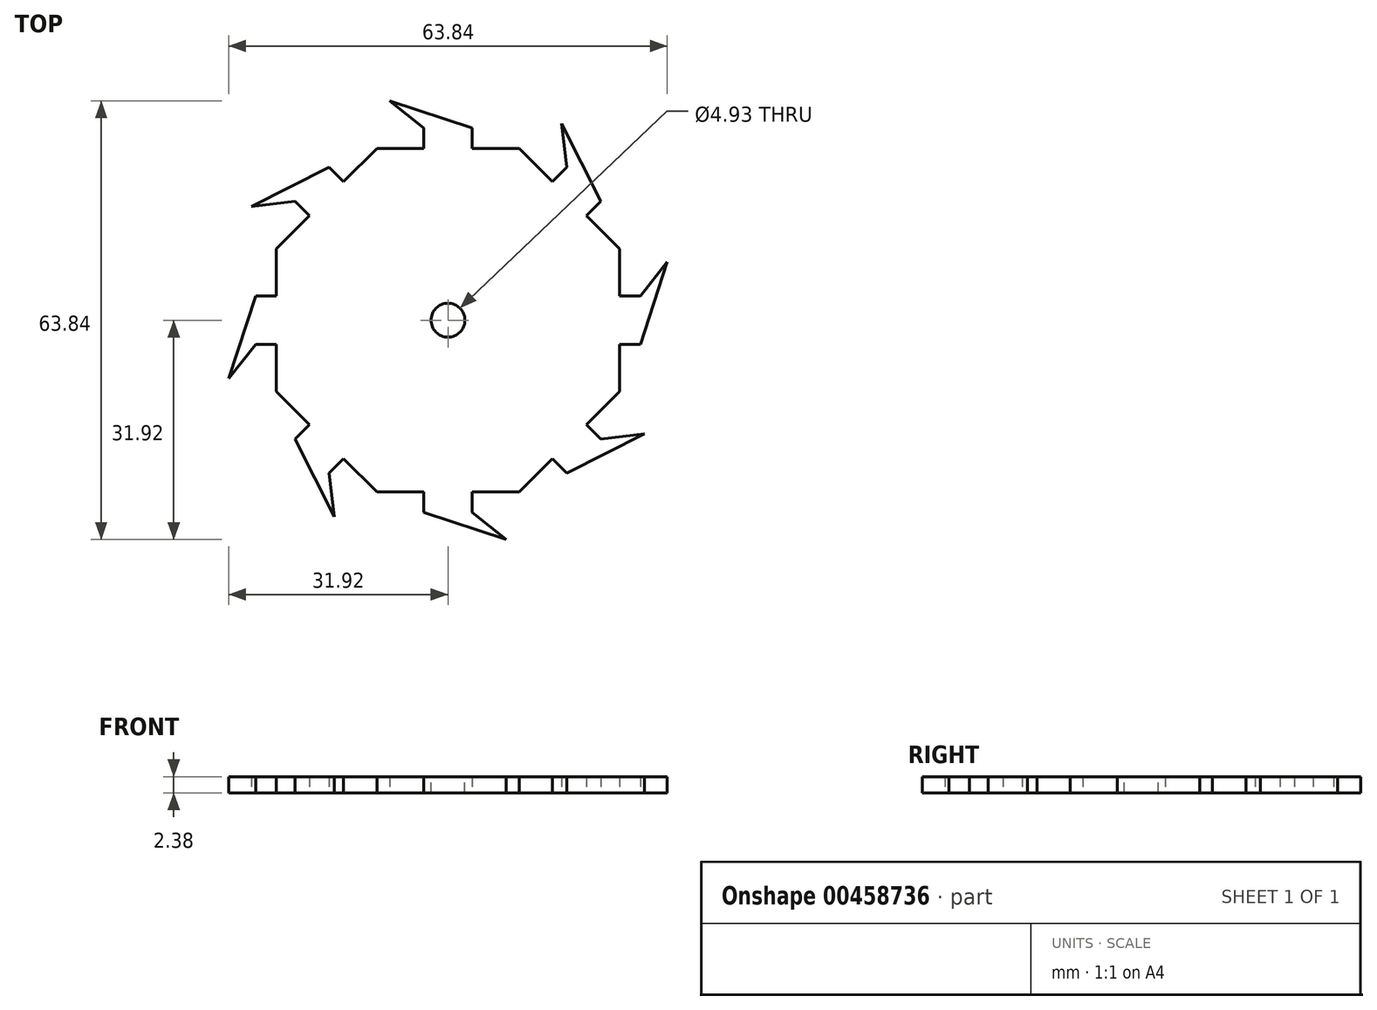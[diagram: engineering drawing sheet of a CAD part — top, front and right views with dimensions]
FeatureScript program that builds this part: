
annotation { "Feature Type Name" : "Feature", "Feature Type Description" : "" }
export const myFeature = defineFeature(function(context is Context, id is Id, definition is map)
    precondition{}
    {
        {
            var Q0;
            Q0=qCreatedBy(makeId("Top.planeOp"),FACE);
            var sketch = newSketch(context, id + "F0", { "sketchPlane" : qUnion([Q0])});
            skLineSegment(sketch, "E0", {"start": v(0, 0) * mm, "end": v(-10.36, 25) * mm});
            skLineSegment(sketch, "E1", {"start": v(0, 0) * mm, "end": v(10.36, 25) * mm});
            skLineSegment(sketch, "E2", {"start": v(-10.36, 25) * mm, "end": v(10.36, 25) * mm});
            skLineSegment(sketch, "E3.bottom", {"start": v(-3.5, 25) * mm, "end": v(3.5, 25) * mm});
            skLineSegment(sketch, "E3.top", {"start": v(-3.5, 28) * mm, "end": v(3.5, 28) * mm});
            skLineSegment(sketch, "E3.left", {"start": v(-3.5, 25) * mm, "end": v(-3.5, 28) * mm});
            skLineSegment(sketch, "E3.right", {"start": v(3.5, 25) * mm, "end": v(3.5, 28) * mm});
            skLineSegment(sketch, "E4", {"start": v(-3.5, 28) * mm, "end": v(-8.5, 31.92) * mm});
            skLineSegment(sketch, "E5", {"start": v(-8.5, 31.92) * mm, "end": v(3.5, 28) * mm});
            skLineSegment(sketch, "E6", {"start": v(0, 0) * mm, "end": v(0, 25) * mm});
            skLineSegment(sketch, "E7.1.0", {"start": v(0, 0) * mm, "end": v(-17.68, 17.68) * mm});
            skLineSegment(sketch, "E7.1.2", {"start": v(0, 0) * mm, "end": v(-25, 10.36) * mm});
            skLineSegment(sketch, "E7.1.3", {"start": v(-28.58, 16.56) * mm, "end": v(-17.32, 22.27) * mm});
            skLineSegment(sketch, "E7.1.4", {"start": v(-15.2, 20.15) * mm, "end": v(-17.32, 22.27) * mm});
            skLineSegment(sketch, "E7.1.5", {"start": v(-22.27, 17.32) * mm, "end": v(-28.58, 16.56) * mm});
            skLineSegment(sketch, "E7.1.6", {"start": v(-20.15, 15.2) * mm, "end": v(-22.27, 17.32) * mm});
            skLineSegment(sketch, "E7.1.7", {"start": v(-25, 10.36) * mm, "end": v(-10.36, 25) * mm});
            skLineSegment(sketch, "E7.1.8", {"start": v(-22.27, 17.32) * mm, "end": v(-17.32, 22.27) * mm});
            skLineSegment(sketch, "E7.1.9", {"start": v(-20.15, 15.2) * mm, "end": v(-15.2, 20.15) * mm});
            skLineSegment(sketch, "E7.2.0", {"start": v(0, 0) * mm, "end": v(-25, 0) * mm});
            skLineSegment(sketch, "E7.2.1", {"start": v(0, 0) * mm, "end": v(-25, 10.36) * mm});
            skLineSegment(sketch, "E7.2.2", {"start": v(0, 0) * mm, "end": v(-25, -10.36) * mm});
            skLineSegment(sketch, "E7.2.3", {"start": v(-31.92, -8.5) * mm, "end": v(-28, 3.5) * mm});
            skLineSegment(sketch, "E7.2.4", {"start": v(-25, 3.5) * mm, "end": v(-28, 3.5) * mm});
            skLineSegment(sketch, "E7.2.5", {"start": v(-28, -3.5) * mm, "end": v(-31.92, -8.5) * mm});
            skLineSegment(sketch, "E7.2.6", {"start": v(-25, -3.5) * mm, "end": v(-28, -3.5) * mm});
            skLineSegment(sketch, "E7.2.7", {"start": v(-25, -10.36) * mm, "end": v(-25, 10.36) * mm});
            skLineSegment(sketch, "E7.2.8", {"start": v(-28, -3.5) * mm, "end": v(-28, 3.5) * mm});
            skLineSegment(sketch, "E7.2.9", {"start": v(-25, -3.5) * mm, "end": v(-25, 3.5) * mm});
            skLineSegment(sketch, "E7.3.0", {"start": v(0, 0) * mm, "end": v(-17.68, -17.68) * mm});
            skLineSegment(sketch, "E7.3.1", {"start": v(0, 0) * mm, "end": v(-25, -10.36) * mm});
            skLineSegment(sketch, "E7.3.2", {"start": v(0, 0) * mm, "end": v(-10.36, -25) * mm});
            skLineSegment(sketch, "E7.3.3", {"start": v(-16.56, -28.58) * mm, "end": v(-22.27, -17.32) * mm});
            skLineSegment(sketch, "E7.3.4", {"start": v(-20.15, -15.2) * mm, "end": v(-22.27, -17.32) * mm});
            skLineSegment(sketch, "E7.3.5", {"start": v(-17.32, -22.27) * mm, "end": v(-16.56, -28.58) * mm});
            skLineSegment(sketch, "E7.3.6", {"start": v(-15.2, -20.15) * mm, "end": v(-17.32, -22.27) * mm});
            skLineSegment(sketch, "E7.3.7", {"start": v(-10.36, -25) * mm, "end": v(-25, -10.36) * mm});
            skLineSegment(sketch, "E7.3.8", {"start": v(-17.32, -22.27) * mm, "end": v(-22.27, -17.32) * mm});
            skLineSegment(sketch, "E7.3.9", {"start": v(-15.2, -20.15) * mm, "end": v(-20.15, -15.2) * mm});
            skLineSegment(sketch, "E7.4.0", {"start": v(0, 0) * mm, "end": v(0, -25) * mm});
            skLineSegment(sketch, "E7.4.1", {"start": v(0, 0) * mm, "end": v(-10.36, -25) * mm});
            skLineSegment(sketch, "E7.4.2", {"start": v(0, 0) * mm, "end": v(10.36, -25) * mm});
            skLineSegment(sketch, "E7.4.3", {"start": v(8.5, -31.92) * mm, "end": v(-3.5, -28) * mm});
            skLineSegment(sketch, "E7.4.4", {"start": v(-3.5, -25) * mm, "end": v(-3.5, -28) * mm});
            skLineSegment(sketch, "E7.4.5", {"start": v(3.5, -28) * mm, "end": v(8.5, -31.92) * mm});
            skLineSegment(sketch, "E7.4.6", {"start": v(3.5, -25) * mm, "end": v(3.5, -28) * mm});
            skLineSegment(sketch, "E7.4.7", {"start": v(10.36, -25) * mm, "end": v(-10.36, -25) * mm});
            skLineSegment(sketch, "E7.4.8", {"start": v(3.5, -28) * mm, "end": v(-3.5, -28) * mm});
            skLineSegment(sketch, "E7.4.9", {"start": v(3.5, -25) * mm, "end": v(-3.5, -25) * mm});
            skLineSegment(sketch, "E7.5.0", {"start": v(0, 0) * mm, "end": v(17.68, -17.68) * mm});
            skLineSegment(sketch, "E7.5.1", {"start": v(0, 0) * mm, "end": v(10.36, -25) * mm});
            skLineSegment(sketch, "E7.5.2", {"start": v(0, 0) * mm, "end": v(25, -10.36) * mm});
            skLineSegment(sketch, "E7.5.3", {"start": v(28.58, -16.56) * mm, "end": v(17.32, -22.27) * mm});
            skLineSegment(sketch, "E7.5.4", {"start": v(15.2, -20.15) * mm, "end": v(17.32, -22.27) * mm});
            skLineSegment(sketch, "E7.5.5", {"start": v(22.27, -17.32) * mm, "end": v(28.58, -16.56) * mm});
            skLineSegment(sketch, "E7.5.6", {"start": v(20.15, -15.2) * mm, "end": v(22.27, -17.32) * mm});
            skLineSegment(sketch, "E7.5.7", {"start": v(25, -10.36) * mm, "end": v(10.36, -25) * mm});
            skLineSegment(sketch, "E7.5.8", {"start": v(22.27, -17.32) * mm, "end": v(17.32, -22.27) * mm});
            skLineSegment(sketch, "E7.5.9", {"start": v(20.15, -15.2) * mm, "end": v(15.2, -20.15) * mm});
            skLineSegment(sketch, "E7.6.0", {"start": v(0, 0) * mm, "end": v(25, 0) * mm});
            skLineSegment(sketch, "E7.6.1", {"start": v(0, 0) * mm, "end": v(25, -10.36) * mm});
            skLineSegment(sketch, "E7.6.2", {"start": v(0, 0) * mm, "end": v(25, 10.36) * mm});
            skLineSegment(sketch, "E7.6.3", {"start": v(31.92, 8.5) * mm, "end": v(28, -3.5) * mm});
            skLineSegment(sketch, "E7.6.4", {"start": v(25, -3.5) * mm, "end": v(28, -3.5) * mm});
            skLineSegment(sketch, "E7.6.5", {"start": v(28, 3.5) * mm, "end": v(31.92, 8.5) * mm});
            skLineSegment(sketch, "E7.6.6", {"start": v(25, 3.5) * mm, "end": v(28, 3.5) * mm});
            skLineSegment(sketch, "E7.6.7", {"start": v(25, 10.36) * mm, "end": v(25, -10.36) * mm});
            skLineSegment(sketch, "E7.6.8", {"start": v(28, 3.5) * mm, "end": v(28, -3.5) * mm});
            skLineSegment(sketch, "E7.6.9", {"start": v(25, 3.5) * mm, "end": v(25, -3.5) * mm});
            skLineSegment(sketch, "E7.7.0", {"start": v(0, 0) * mm, "end": v(17.68, 17.68) * mm});
            skLineSegment(sketch, "E7.7.1", {"start": v(0, 0) * mm, "end": v(25, 10.36) * mm});
            skLineSegment(sketch, "E7.7.3", {"start": v(16.56, 28.58) * mm, "end": v(22.27, 17.32) * mm});
            skLineSegment(sketch, "E7.7.4", {"start": v(20.15, 15.2) * mm, "end": v(22.27, 17.32) * mm});
            skLineSegment(sketch, "E7.7.5", {"start": v(17.32, 22.27) * mm, "end": v(16.56, 28.58) * mm});
            skLineSegment(sketch, "E7.7.6", {"start": v(15.2, 20.15) * mm, "end": v(17.32, 22.27) * mm});
            skLineSegment(sketch, "E7.7.7", {"start": v(10.36, 25) * mm, "end": v(25, 10.36) * mm});
            skLineSegment(sketch, "E7.7.8", {"start": v(17.32, 22.27) * mm, "end": v(22.27, 17.32) * mm});
            skLineSegment(sketch, "E7.7.9", {"start": v(15.2, 20.15) * mm, "end": v(20.15, 15.2) * mm});
            skPoint(sketch, "E7.center", {"position": v(0, 0) * mm});
            skSolve(sketch);
        }
        {
            var Q0;
            Q0 = qSketchRegion(id + "F0", true);
            extrude(context, id + "F1", {"entities" : qUnion([Q0]), "depth" : 2.38 * mm, "offsetDistance" : 25 * mm});
        }
        {
            var Q0;
            Q0=makeQuery(id+"F1.opExtrude","CAP_FACE",FACE,{"disambiguationData":[OSD([sQuery(id+"F0.wireOp",EDGE,"E2"),sQuery(id+"F0.wireOp",EDGE,"E3.left"),sQuery(id+"F0.wireOp",EDGE,"E3.right"),sQuery(id+"F0.wireOp",EDGE,"E4"),sQuery(id+"F0.wireOp",EDGE,"E5"),sQuery(id+"F0.wireOp",EDGE,"E7.1.3"),sQuery(id+"F0.wireOp",EDGE,"E7.1.4"),sQuery(id+"F0.wireOp",EDGE,"E7.1.5"),sQuery(id+"F0.wireOp",EDGE,"E7.1.6"),sQuery(id+"F0.wireOp",EDGE,"E7.1.7"),sQuery(id+"F0.wireOp",EDGE,"E7.2.3"),sQuery(id+"F0.wireOp",EDGE,"E7.2.4"),sQuery(id+"F0.wireOp",EDGE,"E7.2.5"),sQuery(id+"F0.wireOp",EDGE,"E7.2.6"),sQuery(id+"F0.wireOp",EDGE,"E7.2.7"),sQuery(id+"F0.wireOp",EDGE,"E7.3.3"),sQuery(id+"F0.wireOp",EDGE,"E7.3.4"),sQuery(id+"F0.wireOp",EDGE,"E7.3.5"),sQuery(id+"F0.wireOp",EDGE,"E7.3.6"),sQuery(id+"F0.wireOp",EDGE,"E7.3.7"),sQuery(id+"F0.wireOp",EDGE,"E7.4.3"),sQuery(id+"F0.wireOp",EDGE,"E7.4.4"),sQuery(id+"F0.wireOp",EDGE,"E7.4.5"),sQuery(id+"F0.wireOp",EDGE,"E7.4.6"),sQuery(id+"F0.wireOp",EDGE,"E7.4.7"),sQuery(id+"F0.wireOp",EDGE,"E7.5.3"),sQuery(id+"F0.wireOp",EDGE,"E7.5.4"),sQuery(id+"F0.wireOp",EDGE,"E7.5.5"),sQuery(id+"F0.wireOp",EDGE,"E7.5.6"),sQuery(id+"F0.wireOp",EDGE,"E7.5.7"),sQuery(id+"F0.wireOp",EDGE,"E7.6.3"),sQuery(id+"F0.wireOp",EDGE,"E7.6.4"),sQuery(id+"F0.wireOp",EDGE,"E7.6.5"),sQuery(id+"F0.wireOp",EDGE,"E7.6.6"),sQuery(id+"F0.wireOp",EDGE,"E7.6.7"),sQuery(id+"F0.wireOp",EDGE,"E7.7.3"),sQuery(id+"F0.wireOp",EDGE,"E7.7.4"),sQuery(id+"F0.wireOp",EDGE,"E7.7.5"),sQuery(id+"F0.wireOp",EDGE,"E7.7.6"),sQuery(id+"F0.wireOp",EDGE,"E7.7.7")])],"isStart":false});
            var sketch = newSketch(context, id + "F2", { "sketchPlane" : qUnion([Q0])});
            skCircle(sketch, "E8", {"center": v(0, 0) * mm, "radius": 2.46 * mm});
            skSolve(sketch);
        }
        {
            var Q0;
            Q0 = qSketchRegion(id + "F2", true);
            extrude(context, id + "F3", {"entities" : qUnion([Q0]), "operationType" : NewBodyOperationType.REMOVE, "oppositeDirection" : true, "depth" : 25 * mm, "offsetDistance" : 25 * mm});
        }
    });
